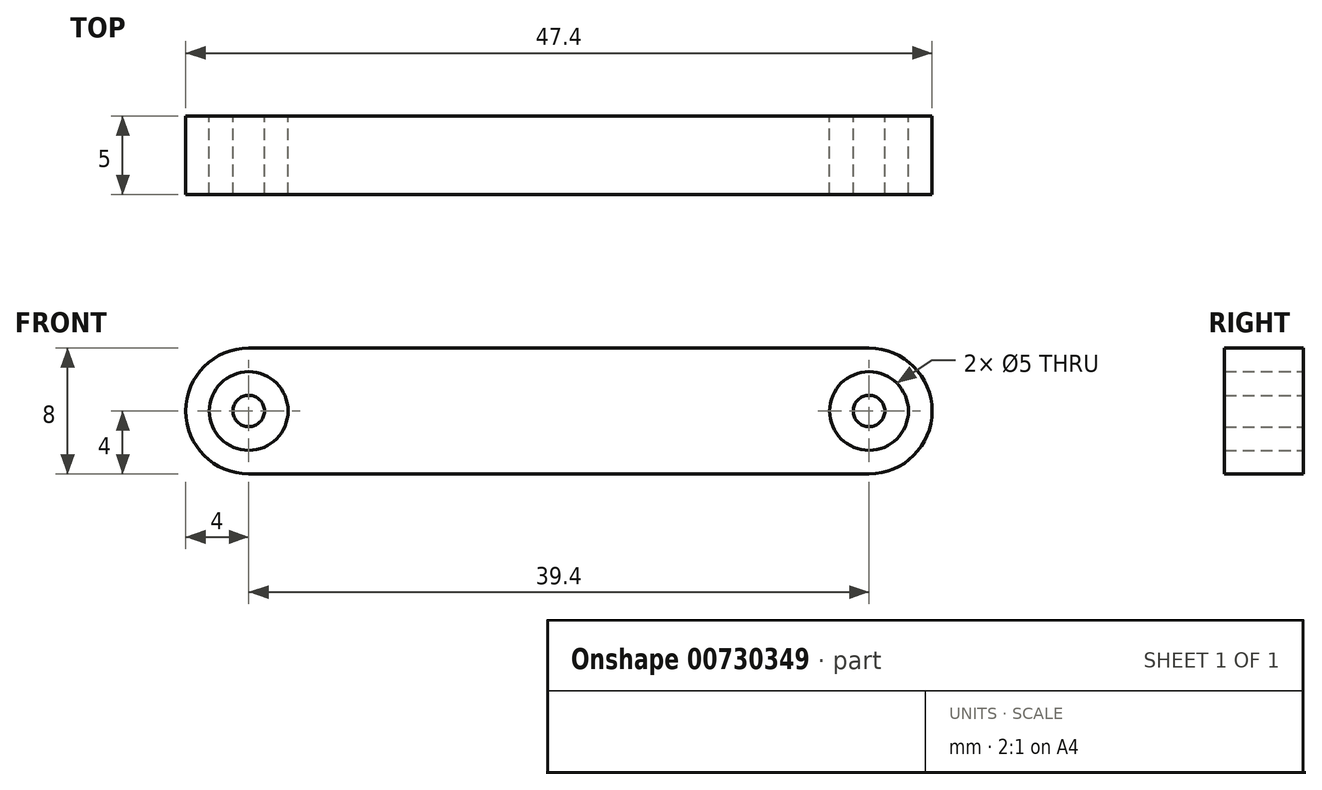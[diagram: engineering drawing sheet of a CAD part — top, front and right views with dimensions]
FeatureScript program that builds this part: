
annotation { "Feature Type Name" : "Feature", "Feature Type Description" : "" }
export const myFeature = defineFeature(function(context is Context, id is Id, definition is map)
    precondition{}
    {
        {
            var Q0;
            Q0=qCreatedBy(makeId("Front.planeOp"),FACE);
            var sketch = newSketch(context, id + "F0", { "sketchPlane" : qUnion([Q0])});
            skArc(sketch, "E0", {"start": v(0, 4) * mm, "mid": v(-4, 0) * mm, "end": v(0, -4) * mm});
            skArc(sketch, "E1", {"start": v(39.4, -4) * mm, "mid": v(43.4, 0) * mm, "end": v(39.4, 4) * mm});
            skCircle(sketch, "E2", {"center": v(0, 0) * mm, "radius": 2.5 * mm});
            skCircle(sketch, "E3", {"center": v(0, 0) * mm, "radius": 1 * mm});
            skCircle(sketch, "E4", {"center": v(39.4, 0) * mm, "radius": 2.5 * mm});
            skCircle(sketch, "E5", {"center": v(39.4, 0) * mm, "radius": 1 * mm});
            skLineSegment(sketch, "E6", {"start": v(0, 4) * mm, "end": v(39.4, 4) * mm});
            skLineSegment(sketch, "E7", {"start": v(0, -4) * mm, "end": v(39.4, -4) * mm});
            skSolve(sketch);
        }
        {
            var Q0;
            Q0 = qSketchRegion(id + "F0", true);
            var Q1;
            Q1=makeQuery(id+"F0.imprint","IMPRINT",FACE,{"disambiguationData":[TD([[makeQuery(id+"F0.imprint","IMPRINT",EDGE,{"derivedFrom":sQuery(id+"F0.wireOp",EDGE,"E5")}),1.0]])]});
            var Q2;
            Q2=makeQuery(id+"F0.imprint","IMPRINT",FACE,{"disambiguationData":[TD([[makeQuery(id+"F0.imprint","IMPRINT",EDGE,{"derivedFrom":sQuery(id+"F0.wireOp",EDGE,"E3")}),1.0]])]});
            extrude(context, id + "F1", {"entities" : qUnion([Q0, Q1, Q2]), "depth" : 5 * mm, "offsetDistance" : 25 * mm});
        }
    });
